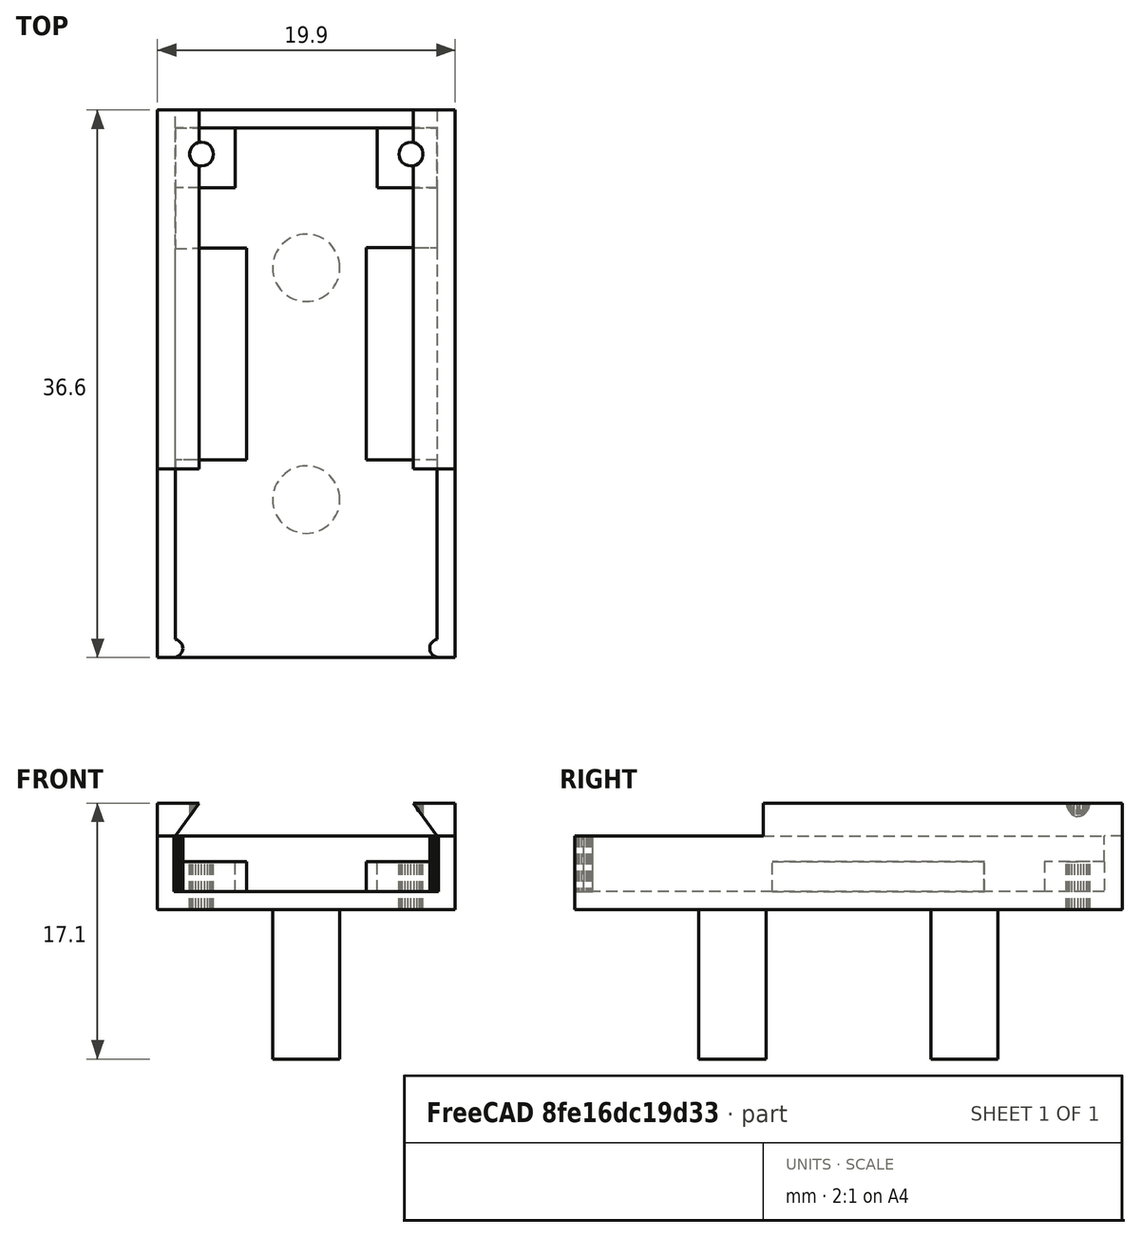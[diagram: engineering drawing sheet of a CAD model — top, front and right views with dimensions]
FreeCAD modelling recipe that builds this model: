
FCSTD DOCUMENT  (FreeCAD 1.0R39109 (Git))
Label: xy-mos-holder
License: All rights reserved
LicenseURL: https://en.wikipedia.org/wiki/All_rights_reserved
objects: Part::Feature×3, Part::Cut×3, Part::Box×2, Part::MultiCommon×2, Mesh::Feature×1, Part::Refine×1, Sketcher::SketchObject×1, Part::Extrusion×1, Part::Fuse×1
note: 15 computed .brp shape members not serialized (recipe doc carries the construction recipe); baked Part::Feature solids carry a one-line shape summary decoded from their .brp

FEATURE [Mesh::Feature] xy_mos_holder  label="xy_mos-holder"
FEATURE [Part::Feature] xy_mos_holder001
  shape: bbox 39.9 x 36.6 x 7.1 mm, 868 faces, 0 solids (baked)
FEATURE [Part::Refine] xy_mos_holder002
  Source = -> xy_mos_holder001
FEATURE [Part::Feature] xy_mos_holder002_solid  label="xy_mos_holder002 (Solid)"
  shape: bbox 39.9 x 36.6 x 7.1 mm, 276 faces (baked)
FEATURE [Part::Box] Box  label="Cube"
  AttacherType = Attacher::AttachEngine3D
  Height = 10
  Length = 10
  Placement = pos=(-11.2,12.1,0) rot=(0,0,1;0rad)
  Width = 10
FEATURE [Part::MultiCommon] Common
  Shapes = -> [xy_mos_holder002_solid,Box]
FEATURE [Part::Feature] xy_mos_holder002_solid001  label="xy_mos_holder002 (Solid)001"
  shape: bbox 39.9 x 36.6 x 7.1 mm, 276 faces (baked)
FEATURE [Part::Cut] Cut  label="xy_mos"
  Base = -> xy_mos_holder002_solid001
  Tool = -> Common
FEATURE [Part::Box] Box001  label="Cube001"
  AttacherType = Attacher::AttachEngine3D
  Height = 10
  Length = 10
  Placement = pos=(18.7,12.1,0) rot=(0,0,1;0rad)
  Width = 10
FEATURE [Part::Cut] Cut001  label="xy_mos001"
  Base = -> xy_mos_holder002_solid001
  Tool = -> Common
FEATURE [Part::MultiCommon] Common001
  Shapes = -> [Cut001,Box001]
FEATURE [Part::Cut] Cut002
  Base = -> Cut
  Tool = -> Common001
FEATURE [Sketcher::SketchObject] Sketch
  ArcFitTolerance = 1e-06
  AttachmentSupport = -> [Cut002]
  ExternalGeometry = -> [Cut002]
  FullyConstrained = true
  MakeInternals = false
  MapMode = 5
  Placement = pos=(0,0,0) rot=(1,0,0;3.14159rad)
  sketch-geometry (2):
    g0: Circle CenterX=8.75 CenterY=-9.35 CenterZ=0 NormalX=0 NormalY=0 NormalZ=1 AngleXU=0 Radius=2.25
    g1: Circle CenterX=8.75 CenterY=-24.85 CenterZ=0 NormalX=0 NormalY=0 NormalZ=1 AngleXU=0 Radius=2.25
  constraints (8):
    c: Diameter(g0) = 4.5
    c: Diameter(g1) = 4.5
    c: Distance(g0,g1) = 15.5
    c: DistanceX(g-3,g-3) = 19.9
    c: Distance(g-3) = 19.9
    c: Distance(g0,g-3) = 10.55
    c: Distance(g0,g-4) = 9.95
    c: Distance(g1,g-8) = 9.95
FEATURE [Part::Extrusion] Extrude
  Base = -> Sketch
  Dir = (0,0,-1)
  DirMode = 2
  FaceMakerClass = Part::FaceMakerBullseye
  FaceMakerMode = 3
  LengthFwd = 10
  LengthRev = 0
  Solid = true
  Symmetric = false
FEATURE [Part::Fuse] Fusion
  Base = -> Cut002
  Tool = -> Extrude
